# Revit family: BP_A0205_Flamco_NexusValveFluctus
name_source: partatom
category: Арматура трубопроводов
units: mm (PartAtom-declared; Revit-internal decimal feet)

## family parameters
Всегда вертикально = Да
На основе рабочей плоскости = Нет
Общий = Да
При загрузке вырезать с полостями = Нет
Размер круглого соединителя = Использовать диаметр
Тип детали = Вставляется

## types (3) — shared parameters
ADSK_Единица измерения = шт.
ADSK_Завод-изготовитель = Flamco
ADSK_Количество = 1
BP_CaseMaterial = BP_SmoothBrass
BP_Category = PipingAccessories
BP_Developer = BIM Project
BP_ID = A0205
BP_Manufacturer = Flamco
BP_OtherMaterial_1 = BP_Plastic_RGB 0 0 0
BP_OtherMaterial_2 = BP_Plastic_RGB 255 0 0
BP_OtherMaterial_3 = BP_Plastic_RGB 0 0 255
BP_SubCategory = BalancingValve
BP_Unit = Pcs.
BP_Version = v1.0
C = 144 мм
H = 75 мм
Изготовитель = Flamco
zero-valued in all types: ADSK_Масса, BP_Mass

## per-type parameters (varying)
| type | A | ADSK_Код изделия | ADSK_Марка | ADSK_Наименование | ADSK_Наименование краткое | ADSK_Обозначение | BP_Article | BP_Designation | BP_MainName | BP_Mark | BP_MassText | BP_NominalDiameter | BP_ShortName | D | D2 | a | Группа модели | Описание |
| Venturi DN 15 L | 61 мм | MN80597.491 | Venturi DN 15 L | Комбинированный статический регулирующий клапан с запорным вентилем, DN 15 L | Комбинированный клапан, DN 15 L | КК - DN 15 L | MN80597.491 | CV - DN 15 L | Combined static circuit control valve with shut-off valve, DN 15 L | Venturi DN 15 L |  | 15 мм | Combined static circuit control valve, DN 15 L | 75 мм | 17 мм | 19 мм | Venturi DN 15 L | Combined static circuit control valve with shut-off valve, DN 15 L |
| Venturi DN 20 L | 65 мм | MN80597.493 | Venturi DN 20L | Комбинированный статический регулирующий клапан с запорным вентилем, DN 20 L | Комбинированный клапан, DN 20 L | КК - DN 20 L | MN80597.493 | CV - DN 20 L | Combined static circuit control valve with shut-off valve, DN 20 L | Venturi DN 20L |  | 20 мм | Combined static circuit control valve, DN 20 L | 78 мм | 19 мм | 20 мм | Venturi DN 20L | Combined static circuit control valve with shut-off valve, DN 20 L |
| Venturi DN 25 S | 78 мм | MN80597.495 | Venturi DN 25 S | Комбинированный статический регулирующий клапан с запорным вентилем, DN 25 S | Комбинированный клапан, DN 25 S | КК - DN 25 S | MN80597.495 | CV - DN 25 S | Combined static circuit control valve with shut-off valve, DN 25 S | Venturi DN 25 S | 0 | 25 мм | Combined static circuit control valve, DN 25 S | 82 мм | 22 мм | 24 мм | Venturi DN 25 S | Combined static circuit control valve with shut-off valve, DN 25 S |
